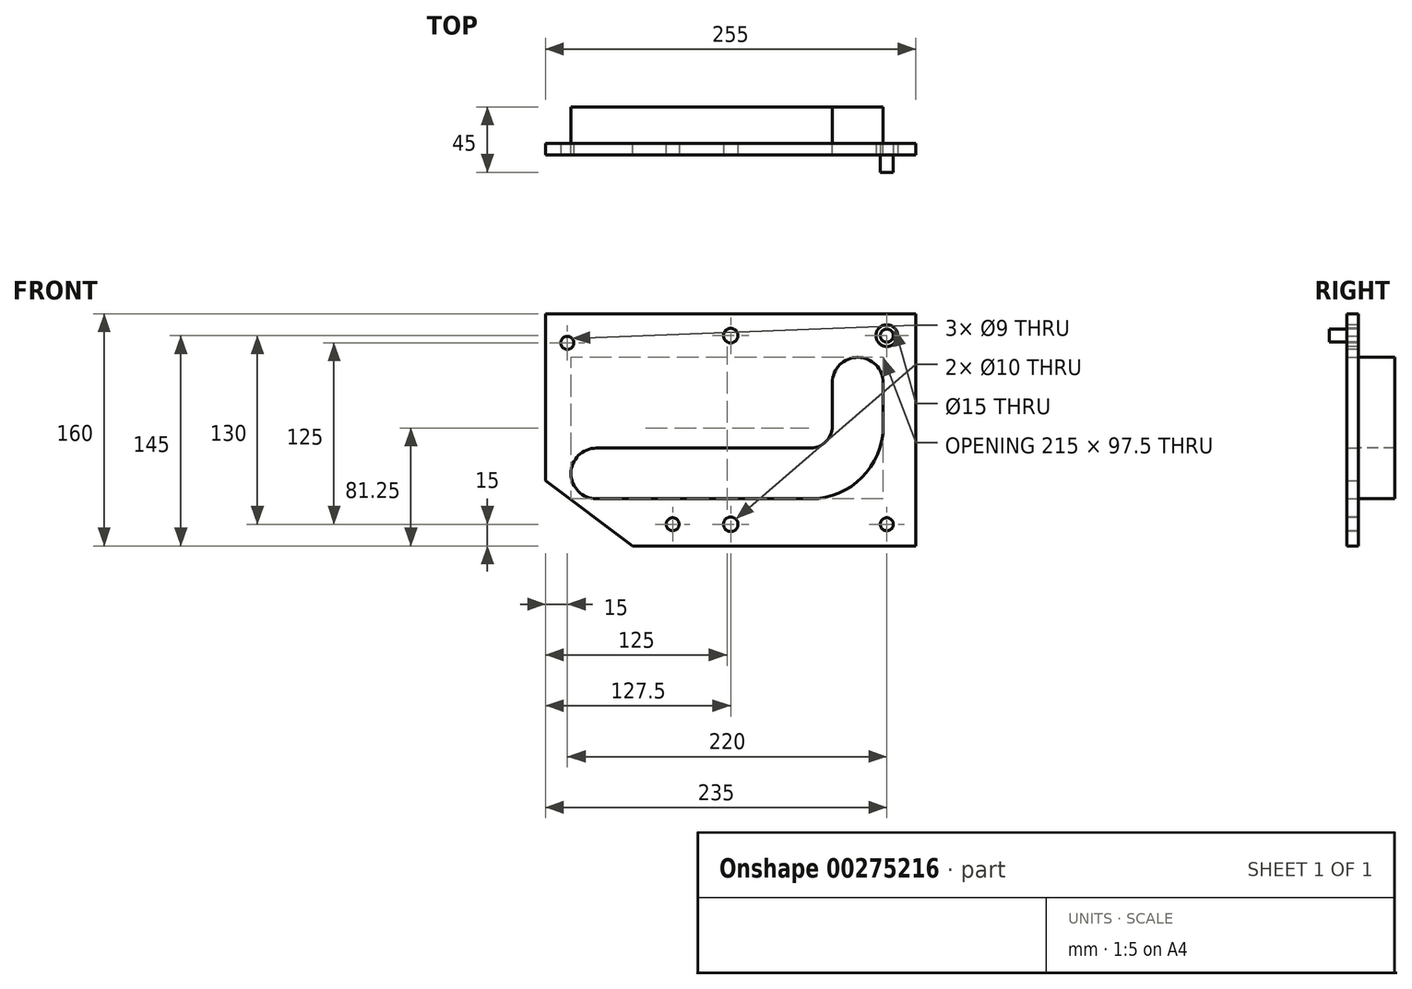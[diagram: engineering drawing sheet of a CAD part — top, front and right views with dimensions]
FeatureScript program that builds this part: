
annotation { "Feature Type Name" : "Feature", "Feature Type Description" : "" }
export const myFeature = defineFeature(function(context is Context, id is Id, definition is map)
    precondition{}
    {
        {
            var Q0;
            Q0=qCreatedBy(makeId("Front.planeOp"),FACE);
            var sketch = newSketch(context, id + "F0", { "sketchPlane" : qUnion([Q0])});
            skLineSegment(sketch, "E0.bottom", {"start": v(60, 0) * mm, "end": v(255, 0) * mm});
            skLineSegment(sketch, "E0.top", {"start": v(0, 160) * mm, "end": v(255, 160) * mm});
            skLineSegment(sketch, "E0.left", {"start": v(0, 45) * mm, "end": v(0, 160) * mm});
            skLineSegment(sketch, "E0.right", {"start": v(255, 0) * mm, "end": v(255, 160) * mm});
            skLineSegment(sketch, "E1", {"start": v(0, 45) * mm, "end": v(60, 0) * mm});
            skPoint(sketch, "E2.orphan", {"position": v(0, 0) * mm});
            skLineSegment(sketch, "E3", {"start": v(35, 67.5) * mm, "end": v(182.5, 67.5) * mm});
            skLineSegment(sketch, "E4", {"start": v(197.5, 112.5) * mm, "end": v(197.5, 82.5) * mm});
            skLineSegment(sketch, "E5", {"start": v(232.5, 112.5) * mm, "end": v(232.5, 82.5) * mm});
            skLineSegment(sketch, "E6", {"start": v(35, 32.5) * mm, "end": v(182.5, 32.5) * mm});
            skArc(sketch, "E7", {"start": v(232.5, 82.5) * mm, "mid": v(217.86, 47.14) * mm, "end": v(182.5, 32.5) * mm});
            skArc(sketch, "E8", {"start": v(182.5, 67.5) * mm, "mid": v(193.1, 71.9) * mm, "end": v(197.5, 82.5) * mm});
            skLineSegment(sketch, "E9", {"start": v(20.85, 50) * mm, "end": v(215, 50) * mm, "construction": true});
            skLineSegment(sketch, "E10", {"start": v(215, 50) * mm, "end": v(215, 142.75) * mm, "construction": true});
            skArc(sketch, "E11", {"start": v(35, 67.5) * mm, "mid": v(17.5, 50) * mm, "end": v(35, 32.5) * mm});
            skArc(sketch, "E12", {"start": v(232.5, 112.5) * mm, "mid": v(215, 130) * mm, "end": v(197.5, 112.5) * mm});
            skSolve(sketch);
        }
        {
            var Q0;
            Q0=makeQuery(id+"F0.imprint","IMPRINT",FACE,{"disambiguationData":[TD([[makeQuery(id+"F0.imprint","IMPRINT",EDGE,{"derivedFrom":sQuery(id+"F0.wireOp",EDGE,"E0.bottom")}),1.0]])]});
            extrude(context, id + "F1", {"entities" : qUnion([Q0]), "depth" : 20 * mm});
        }
        {
            var Q0;
            Q0=makeQuery(id+"F1.opExtrude","CAP_FACE",FACE,{"disambiguationData":[OSD([sQuery(id+"F0.wireOp",EDGE,"E0.bottom"),sQuery(id+"F0.wireOp",EDGE,"E0.top"),sQuery(id+"F0.wireOp",EDGE,"E0.left"),sQuery(id+"F0.wireOp",EDGE,"E0.right"),sQuery(id+"F0.wireOp",EDGE,"E1"),sQuery(id+"F0.wireOp",EDGE,"E3"),sQuery(id+"F0.wireOp",EDGE,"E4"),sQuery(id+"F0.wireOp",EDGE,"E5"),sQuery(id+"F0.wireOp",EDGE,"E6"),sQuery(id+"F0.wireOp",EDGE,"E7"),sQuery(id+"F0.wireOp",EDGE,"E8"),sQuery(id+"F0.wireOp",EDGE,"E11"),sQuery(id+"F0.wireOp",EDGE,"E12")])],"isStart":false});
            var sketch = newSketch(context, id + "F2", { "sketchPlane" : qUnion([Q0])});
            skCircle(sketch, "E13", {"center": v(87.5, 15) * mm, "radius": 4.5 * mm});
            skCircle(sketch, "E14", {"center": v(87.5, 15) * mm, "radius": 7.5 * mm});
            skCircle(sketch, "E15", {"center": v(235, 15) * mm, "radius": 4.5 * mm});
            skCircle(sketch, "E16", {"center": v(235, 15) * mm, "radius": 7.5 * mm});
            skLineSegment(sketch, "E17", {"start": v(-57.17, 80) * mm, "end": v(298.19, 80) * mm, "construction": true});
            skCircle(sketch, "E18.MirrorC", {"center": v(235, 145) * mm, "radius": 7.5 * mm});
            skCircle(sketch, "E19.MirrorC", {"center": v(235, 145) * mm, "radius": 4.5 * mm});
            skPoint(sketch, "E20", {"position": v(127.5, 15) * mm});
            skPoint(sketch, "E21.MirrorP", {"position": v(127.5, 145) * mm});
            skCircle(sketch, "E22", {"center": v(15, 140) * mm, "radius": 4.5 * mm});
            skCircle(sketch, "E23", {"center": v(15, 140) * mm, "radius": 7.5 * mm});
            skSolve(sketch);
        }
        {
            var Q0;
            Q0=makeQuery(id+"F2.imprint","IMPRINT",FACE,{"disambiguationData":[TD([[makeQuery(id+"F2.imprint","IMPRINT",EDGE,{"derivedFrom":sQuery(id+"F2.wireOp",EDGE,"E22")}),1.0]])]});
            var Q1;
            Q1=makeQuery(id+"F2.imprint","IMPRINT",FACE,{"disambiguationData":[TD([[makeQuery(id+"F2.imprint","IMPRINT",EDGE,{"derivedFrom":sQuery(id+"F2.wireOp",EDGE,"E19.MirrorC")}),-1.0]])]});
            var Q2;
            Q2=makeQuery(id+"F2.imprint","IMPRINT",FACE,{"disambiguationData":[TD([[makeQuery(id+"F2.imprint","IMPRINT",EDGE,{"derivedFrom":sQuery(id+"F2.wireOp",EDGE,"E15")}),1.0]])]});
            var Q3;
            Q3=makeQuery(id+"F2.imprint","IMPRINT",FACE,{"disambiguationData":[TD([[makeQuery(id+"F2.imprint","IMPRINT",EDGE,{"derivedFrom":sQuery(id+"F2.wireOp",EDGE,"E13")}),1.0]])]});
            extrude(context, id + "F3", {"entities" : qUnion([Q0, Q1, Q2, Q3]), "operationType" : NewBodyOperationType.REMOVE, "endBound" : BoundingType.THROUGH_ALL, "oppositeDirection" : true, "depth" : 25 * mm});
        }
        {
            var Q0;
            Q0=makeQuery(id+"F2.imprint","IMPRINT",FACE,{"disambiguationData":[TD([[makeQuery(id+"F2.imprint","IMPRINT",EDGE,{"derivedFrom":sQuery(id+"F2.wireOp",EDGE,"E22")}),-1.0]])]});
            var Q1;
            Q1=makeQuery(id+"F2.imprint","IMPRINT",FACE,{"disambiguationData":[TD([[makeQuery(id+"F2.imprint","IMPRINT",EDGE,{"derivedFrom":sQuery(id+"F2.wireOp",EDGE,"E18.MirrorC")}),-1.0]])]});
            var Q2;
            Q2=makeQuery(id+"F2.imprint","IMPRINT",FACE,{"disambiguationData":[TD([[makeQuery(id+"F2.imprint","IMPRINT",EDGE,{"derivedFrom":sQuery(id+"F2.wireOp",EDGE,"E15")}),-1.0]])]});
            var Q3;
            Q3=makeQuery(id+"F2.imprint","IMPRINT",FACE,{"disambiguationData":[TD([[makeQuery(id+"F2.imprint","IMPRINT",EDGE,{"derivedFrom":sQuery(id+"F2.wireOp",EDGE,"E13")}),-1.0]])]});
            extrude(context, id + "F4", {"entities" : qUnion([Q0, Q1, Q2, Q3]), "operationType" : NewBodyOperationType.REMOVE, "oppositeDirection" : true, "depth" : 12 * mm});
        }
        {
            var Q0;
            Q0=sQuery(id+"F2.wireOp",VERTEX,"E21.MirrorP");
            var Q1;
            Q1=sQuery(id+"F2.wireOp",VERTEX,"E20");
            var Q2;
            Q2=makeQuery(id+"F1.opExtrude","SWEPT_BODY",BODY,{"disambiguationData":[OSD([sQuery(id+"F0.wireOp",EDGE,"E0.bottom"),sQuery(id+"F0.wireOp",EDGE,"E0.top"),sQuery(id+"F0.wireOp",EDGE,"E0.left"),sQuery(id+"F0.wireOp",EDGE,"E0.right"),sQuery(id+"F0.wireOp",EDGE,"E1"),sQuery(id+"F0.wireOp",EDGE,"E3"),sQuery(id+"F0.wireOp",EDGE,"E4"),sQuery(id+"F0.wireOp",EDGE,"E5"),sQuery(id+"F0.wireOp",EDGE,"E6"),sQuery(id+"F0.wireOp",EDGE,"E7"),sQuery(id+"F0.wireOp",EDGE,"E8"),sQuery(id+"F0.wireOp",EDGE,"E11"),sQuery(id+"F0.wireOp",EDGE,"E12")])]});
            hole(context, id + "F5", {"style" : HoleStyle.SIMPLE, "endStyle" : HoleEndStyle.THROUGH, "holeDiameter" : 10 * mm, "tappedDepth" : 12 * mm, "tapClearance" : 3, "locations" : qUnion([Q0, Q1]), "scope" : qUnion([Q2])});
        }
        {
            var Q0;
            Q0=makeQuery(id+"F1.opExtrude","CAP_FACE",FACE,{"disambiguationData":[OSD([sQuery(id+"F0.wireOp",EDGE,"E0.bottom"),sQuery(id+"F0.wireOp",EDGE,"E0.top"),sQuery(id+"F0.wireOp",EDGE,"E0.left"),sQuery(id+"F0.wireOp",EDGE,"E0.right"),sQuery(id+"F0.wireOp",EDGE,"E1"),sQuery(id+"F0.wireOp",EDGE,"E3"),sQuery(id+"F0.wireOp",EDGE,"E4"),sQuery(id+"F0.wireOp",EDGE,"E5"),sQuery(id+"F0.wireOp",EDGE,"E6"),sQuery(id+"F0.wireOp",EDGE,"E7"),sQuery(id+"F0.wireOp",EDGE,"E8"),sQuery(id+"F0.wireOp",EDGE,"E11"),sQuery(id+"F0.wireOp",EDGE,"E12")])],"isStart":true});
            var sketch = newSketch(context, id + "F6", { "sketchPlane" : qUnion([Q0])});
            skLineSegment(sketch, "E24.0", {"start": v(-35, 67.5) * mm, "end": v(-182.5, 67.5) * mm});
            skLineSegment(sketch, "E24.1", {"start": v(-35, 32.5) * mm, "end": v(-182.5, 32.5) * mm});
            skArc(sketch, "E24.2", {"start": v(-35, 67.5) * mm, "mid": v(-17.5, 50) * mm, "end": v(-35, 32.5) * mm});
            skPoint(sketch, "E24.3", {"position": v(-197.5, 112.5) * mm});
            skLineSegment(sketch, "E24.4", {"start": v(-197.5, 112.5) * mm, "end": v(-197.5, 82.5) * mm});
            skArc(sketch, "E24.5", {"start": v(-232.5, 112.5) * mm, "mid": v(-215, 130) * mm, "end": v(-197.5, 112.5) * mm});
            skLineSegment(sketch, "E24.6", {"start": v(-232.5, 112.5) * mm, "end": v(-232.5, 82.5) * mm});
            skArc(sketch, "E24.7", {"start": v(-232.5, 82.5) * mm, "mid": v(-217.86, 47.14) * mm, "end": v(-182.5, 32.5) * mm});
            skArc(sketch, "E24.8", {"start": v(-182.5, 67.5) * mm, "mid": v(-193.1, 71.9) * mm, "end": v(-197.5, 82.5) * mm});
            skPoint(sketch, "E24.9", {"position": v(-193.1, 71.9) * mm});
            skSolve(sketch);
        }
        {
            var Q0;
            Q0 = qSketchRegion(id + "F6", true);
            extrude(context, id + "F7", {"entities" : qUnion([Q0]), "depth" : 25 * mm});
        }
    });
